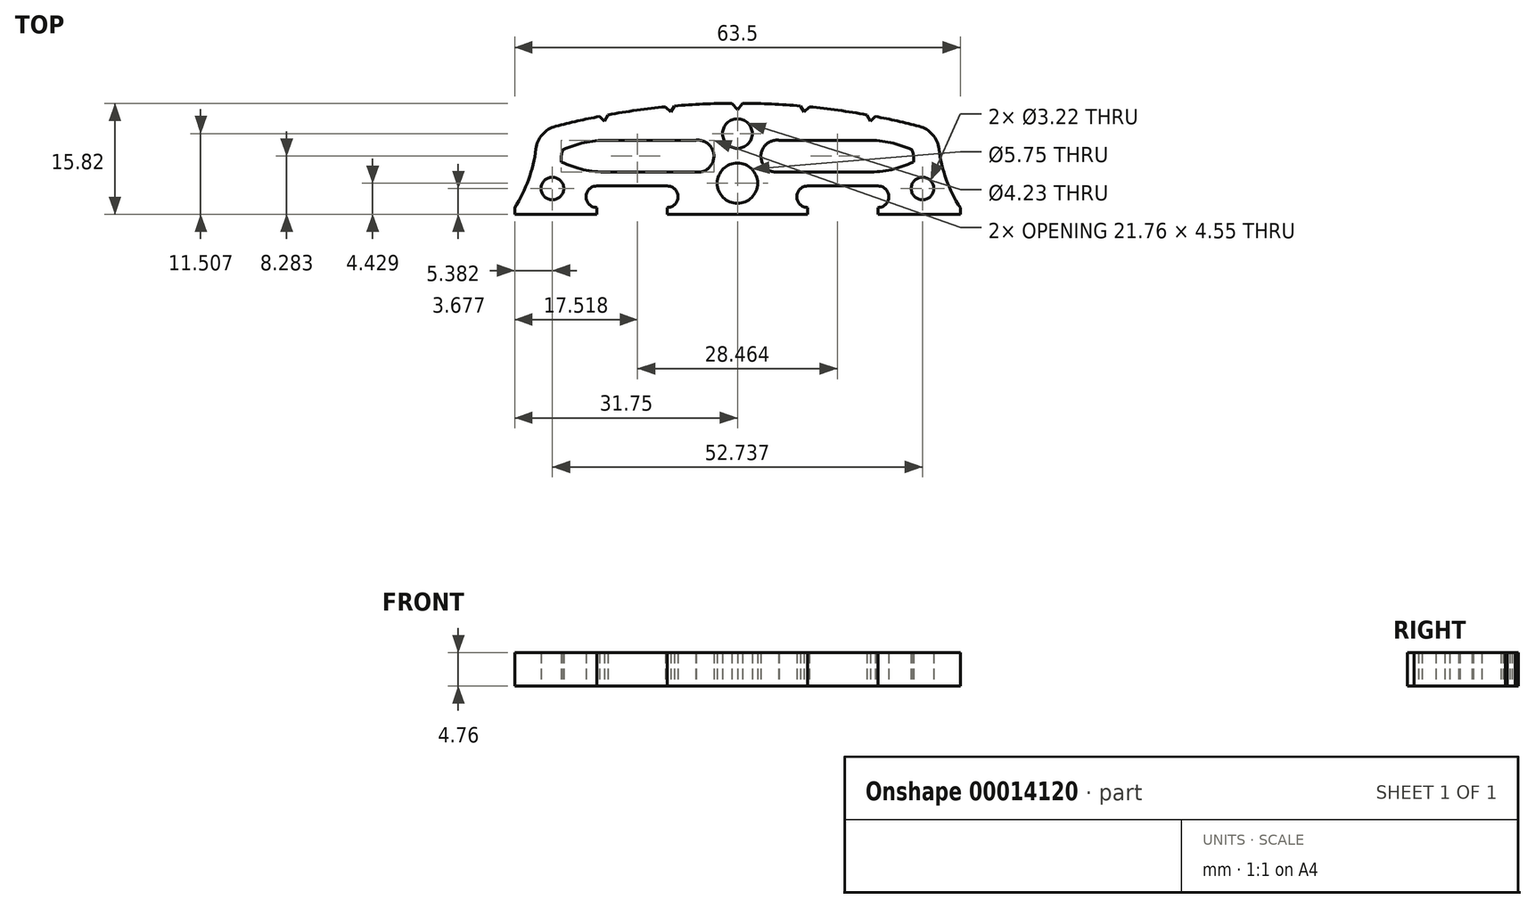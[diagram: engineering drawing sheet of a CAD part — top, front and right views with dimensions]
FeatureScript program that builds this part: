
annotation { "Feature Type Name" : "Feature", "Feature Type Description" : "" }
export const myFeature = defineFeature(function(context is Context, id is Id, definition is map)
    precondition{}
    {
        {
            var Q0;
            Q0=qCreatedBy(makeId("Top.planeOp"),FACE);
            var sketch = newSketch(context, id + "F0", { "sketchPlane" : qUnion([Q0])});
            skArc(sketch, "E0", {"start": v(28.57, 22.8) * mm, "mid": v(0, 26.8) * mm, "end": v(-28.58, 22.8) * mm});
            skLineSegment(sketch, "E1", {"start": v(-31.75, 11.91) * mm, "end": v(-31.75, 10.98) * mm});
            skLineSegment(sketch, "E2", {"start": v(-31.75, 10.98) * mm, "end": v(-20.04, 10.98) * mm});
            skLineSegment(sketch, "E3", {"start": v(-20.04, 10.98) * mm, "end": v(-20.04, 11.95) * mm});
            skLineSegment(sketch, "E4.0.MirrorCS", {"start": v(31.75, 10.98) * mm, "end": v(20.04, 10.98) * mm});
            skLineSegment(sketch, "E5.0.MirrorCS", {"start": v(20.04, 10.98) * mm, "end": v(20.04, 11.95) * mm});
            skLineSegment(sketch, "E6.0.MirrorCS", {"start": v(31.75, 11.91) * mm, "end": v(31.75, 10.98) * mm});
            skLineSegment(sketch, "E7.bottom", {"start": v(-20.04, 11.95) * mm, "end": v(-10, 11.95) * mm});
            skLineSegment(sketch, "E7.top", {"start": v(-20.04, 15) * mm, "end": v(-10, 15) * mm});
            skLineSegment(sketch, "E8.0.MirrorCS", {"start": v(20.04, 15) * mm, "end": v(10, 15) * mm});
            skLineSegment(sketch, "E9.0.MirrorCS", {"start": v(20.04, 11.95) * mm, "end": v(10, 11.95) * mm});
            skArc(sketch, "E10", {"start": v(-20.04, 15) * mm, "mid": v(-21.57, 13.48) * mm, "end": v(-20.04, 11.95) * mm});
            skArc(sketch, "E11", {"start": v(-10, 11.95) * mm, "mid": v(-8.47, 13.48) * mm, "end": v(-10, 15) * mm});
            skArc(sketch, "E12", {"start": v(10, 15) * mm, "mid": v(8.47, 13.48) * mm, "end": v(10, 11.95) * mm});
            skArc(sketch, "E13", {"start": v(20.04, 11.95) * mm, "mid": v(21.57, 13.48) * mm, "end": v(20.04, 15) * mm});
            skArc(sketch, "E14", {"start": v(-31.75, 11.91) * mm, "mid": v(-29.38, 17.13) * mm, "end": v(-28.58, 22.8) * mm});
            skArc(sketch, "E15.0.MirrorCS", {"start": v(31.75, 11.91) * mm, "mid": v(29.38, 17.13) * mm, "end": v(28.58, 22.8) * mm});
            skLineSegment(sketch, "E16.top", {"start": v(-10, 10.98) * mm, "end": v(10, 10.98) * mm});
            skLineSegment(sketch, "E16.left", {"start": v(-10, 11.95) * mm, "end": v(-10, 10.98) * mm});
            skLineSegment(sketch, "E16.right", {"start": v(10, 11.95) * mm, "end": v(10, 10.98) * mm});
            skLineSegment(sketch, "E17", {"start": v(-0.77, 26.8) * mm, "end": v(0, 25.89) * mm});
            skLineSegment(sketch, "E18", {"start": v(0, 25.89) * mm, "end": v(0.72, 26.8) * mm});
            skLineSegment(sketch, "E19", {"start": v(9.52, 25.6) * mm, "end": v(10.24, 26.3) * mm});
            skLineSegment(sketch, "E20", {"start": v(9.52, 25.6) * mm, "end": v(9, 26.41) * mm});
            skLineSegment(sketch, "E21.0.MirrorCS", {"start": v(-9.52, 25.6) * mm, "end": v(-10.24, 26.3) * mm});
            skLineSegment(sketch, "E22.0.MirrorCS", {"start": v(-9.52, 25.6) * mm, "end": v(-9, 26.41) * mm});
            skLineSegment(sketch, "E23", {"start": v(18.95, 24.26) * mm, "end": v(19.66, 24.93) * mm});
            skLineSegment(sketch, "E24", {"start": v(18.95, 24.26) * mm, "end": v(18.44, 25.16) * mm});
            skLineSegment(sketch, "E25.0.MirrorCS", {"start": v(-18.95, 24.26) * mm, "end": v(-19.66, 24.93) * mm});
            skLineSegment(sketch, "E26.0.MirrorCS", {"start": v(-18.95, 24.26) * mm, "end": v(-18.44, 25.16) * mm});
            skArc(sketch, "E27", {"start": v(-24.86, 20.2) * mm, "mid": v(-25.1, 19.33) * mm, "end": v(-25.07, 18.43) * mm});
            skArc(sketch, "E28", {"start": v(-18.64, 21.54) * mm, "mid": v(-21.82, 21.2) * mm, "end": v(-24.86, 20.2) * mm});
            skArc(sketch, "E29", {"start": v(-25.07, 18.43) * mm, "mid": v(-21.93, 17.35) * mm, "end": v(-18.64, 16.99) * mm});
            skArc(sketch, "E30.0.MirrorCS", {"start": v(25.07, 18.43) * mm, "mid": v(21.93, 17.35) * mm, "end": v(18.64, 16.99) * mm});
            skArc(sketch, "E31.0.MirrorCS", {"start": v(18.64, 21.54) * mm, "mid": v(21.82, 21.2) * mm, "end": v(24.86, 20.2) * mm});
            skArc(sketch, "E32.0.MirrorCS", {"start": v(24.86, 20.2) * mm, "mid": v(25.1, 19.33) * mm, "end": v(25.07, 18.43) * mm});
            skArc(sketch, "E33", {"start": v(-5.89, 16.99) * mm, "mid": v(-3.35, 19.3) * mm, "end": v(-5.96, 21.54) * mm});
            skArc(sketch, "E34.0.MirrorCS", {"start": v(5.89, 16.99) * mm, "mid": v(3.35, 19.3) * mm, "end": v(5.96, 21.54) * mm});
            skLineSegment(sketch, "E35", {"start": v(-18.64, 21.54) * mm, "end": v(-5.96, 21.54) * mm});
            skLineSegment(sketch, "E36", {"start": v(-5.89, 16.99) * mm, "end": v(-18.64, 16.99) * mm});
            skLineSegment(sketch, "E37", {"start": v(5.96, 21.54) * mm, "end": v(18.64, 21.54) * mm});
            skLineSegment(sketch, "E38", {"start": v(5.89, 16.99) * mm, "end": v(18.64, 16.99) * mm});
            skCircle(sketch, "E39", {"center": v(0, 15.4) * mm, "radius": 2.88 * mm});
            skCircle(sketch, "E40", {"center": v(-26.37, 14.66) * mm, "radius": 1.61 * mm});
            skCircle(sketch, "E41.0.MirrorC", {"center": v(26.37, 14.66) * mm, "radius": 1.61 * mm});
            skSolve(sketch);
        }
        {
            var Q0;
            Q0=makeQuery(id+"F0.imprint","IMPRINT",FACE,{"disambiguationData":[TD([[makeQuery(id+"F0.imprint","IMPRINT",EDGE,{"derivedFrom":sQuery(id+"F0.wireOp",EDGE,"E0")}),1.0]])]});
            extrude(context, id + "F1", {"entities" : qUnion([Q0]), "depth" : 4.76 * mm});
        }
        {
            var Q0;
            Q0=makeQuery(id+"F1.opExtrude","SWEPT_EDGE",EDGE,{"disambiguationData":[OSD([sQuery(id+"F0.wireOp",EDGE,"E0"),sQuery(id+"F0.wireOp",EDGE,"E15.0.MirrorCS")])]});
            var Q1;
            Q1=makeQuery(id+"F1.opExtrude","SWEPT_EDGE",EDGE,{"disambiguationData":[OSD([sQuery(id+"F0.wireOp",EDGE,"E0"),sQuery(id+"F0.wireOp",EDGE,"E14")])]});
            fillet(context, id + "F2", {"entities" : qUnion([Q0, Q1]), "radius" : 3.8 * mm, "tangentPropagation" : true, "allowEdgeOverflow" : false});
        }
        {
            var Q0;
            Q0=makeQuery(id+"F1.opExtrude","CAP_FACE",FACE,{"disambiguationData":[OSD([sQuery(id+"F0.wireOp",EDGE,"E0"),sQuery(id+"F0.wireOp",EDGE,"E1"),sQuery(id+"F0.wireOp",EDGE,"E2"),sQuery(id+"F0.wireOp",EDGE,"E3"),sQuery(id+"F0.wireOp",EDGE,"E4.0.MirrorCS"),sQuery(id+"F0.wireOp",EDGE,"E5.0.MirrorCS"),sQuery(id+"F0.wireOp",EDGE,"E6.0.MirrorCS"),sQuery(id+"F0.wireOp",EDGE,"E7.top"),sQuery(id+"F0.wireOp",EDGE,"E8.0.MirrorCS"),sQuery(id+"F0.wireOp",EDGE,"E10"),sQuery(id+"F0.wireOp",EDGE,"E11"),sQuery(id+"F0.wireOp",EDGE,"E12"),sQuery(id+"F0.wireOp",EDGE,"E13"),sQuery(id+"F0.wireOp",EDGE,"E14"),sQuery(id+"F0.wireOp",EDGE,"E15.0.MirrorCS"),sQuery(id+"F0.wireOp",EDGE,"E16.top"),sQuery(id+"F0.wireOp",EDGE,"E16.left"),sQuery(id+"F0.wireOp",EDGE,"E16.right"),sQuery(id+"F0.wireOp",EDGE,"E17"),sQuery(id+"F0.wireOp",EDGE,"E18"),sQuery(id+"F0.wireOp",EDGE,"E19"),sQuery(id+"F0.wireOp",EDGE,"E20"),sQuery(id+"F0.wireOp",EDGE,"E21.0.MirrorCS"),sQuery(id+"F0.wireOp",EDGE,"E22.0.MirrorCS"),sQuery(id+"F0.wireOp",EDGE,"E23"),sQuery(id+"F0.wireOp",EDGE,"E24"),sQuery(id+"F0.wireOp",EDGE,"E25.0.MirrorCS"),sQuery(id+"F0.wireOp",EDGE,"E26.0.MirrorCS"),sQuery(id+"F0.wireOp",EDGE,"E27"),sQuery(id+"F0.wireOp",EDGE,"E28"),sQuery(id+"F0.wireOp",EDGE,"E29"),sQuery(id+"F0.wireOp",EDGE,"E30.0.MirrorCS"),sQuery(id+"F0.wireOp",EDGE,"E31.0.MirrorCS"),sQuery(id+"F0.wireOp",EDGE,"E32.0.MirrorCS"),sQuery(id+"F0.wireOp",EDGE,"E33"),sQuery(id+"F0.wireOp",EDGE,"E34.0.MirrorCS"),sQuery(id+"F0.wireOp",EDGE,"E35"),sQuery(id+"F0.wireOp",EDGE,"E36"),sQuery(id+"F0.wireOp",EDGE,"E37"),sQuery(id+"F0.wireOp",EDGE,"E38"),sQuery(id+"F0.wireOp",EDGE,"E39"),sQuery(id+"F0.wireOp",EDGE,"E40"),sQuery(id+"F0.wireOp",EDGE,"E41.0.MirrorC")])],"isStart":true});
            var sketch = newSketch(context, id + "F3", { "sketchPlane" : qUnion([Q0])});
            skCircle(sketch, "E42", {"center": v(0, -22.49) * mm, "radius": 2.12 * mm});
            skSolve(sketch);
        }
        {
            var Q0;
            Q0=makeQuery(id+"F3.imprint","IMPRINT",FACE,{"disambiguationData":[TD([[makeQuery(id+"F3.imprint","IMPRINT",EDGE,{"derivedFrom":sQuery(id+"F3.wireOp",EDGE,"E42")}),1.0]])]});
            extrude(context, id + "F4", {"entities" : qUnion([Q0]), "operationType" : NewBodyOperationType.REMOVE, "endBound" : BoundingType.UP_TO_NEXT, "oppositeDirection" : true, "depth" : 25.4 * mm});
        }
    });
